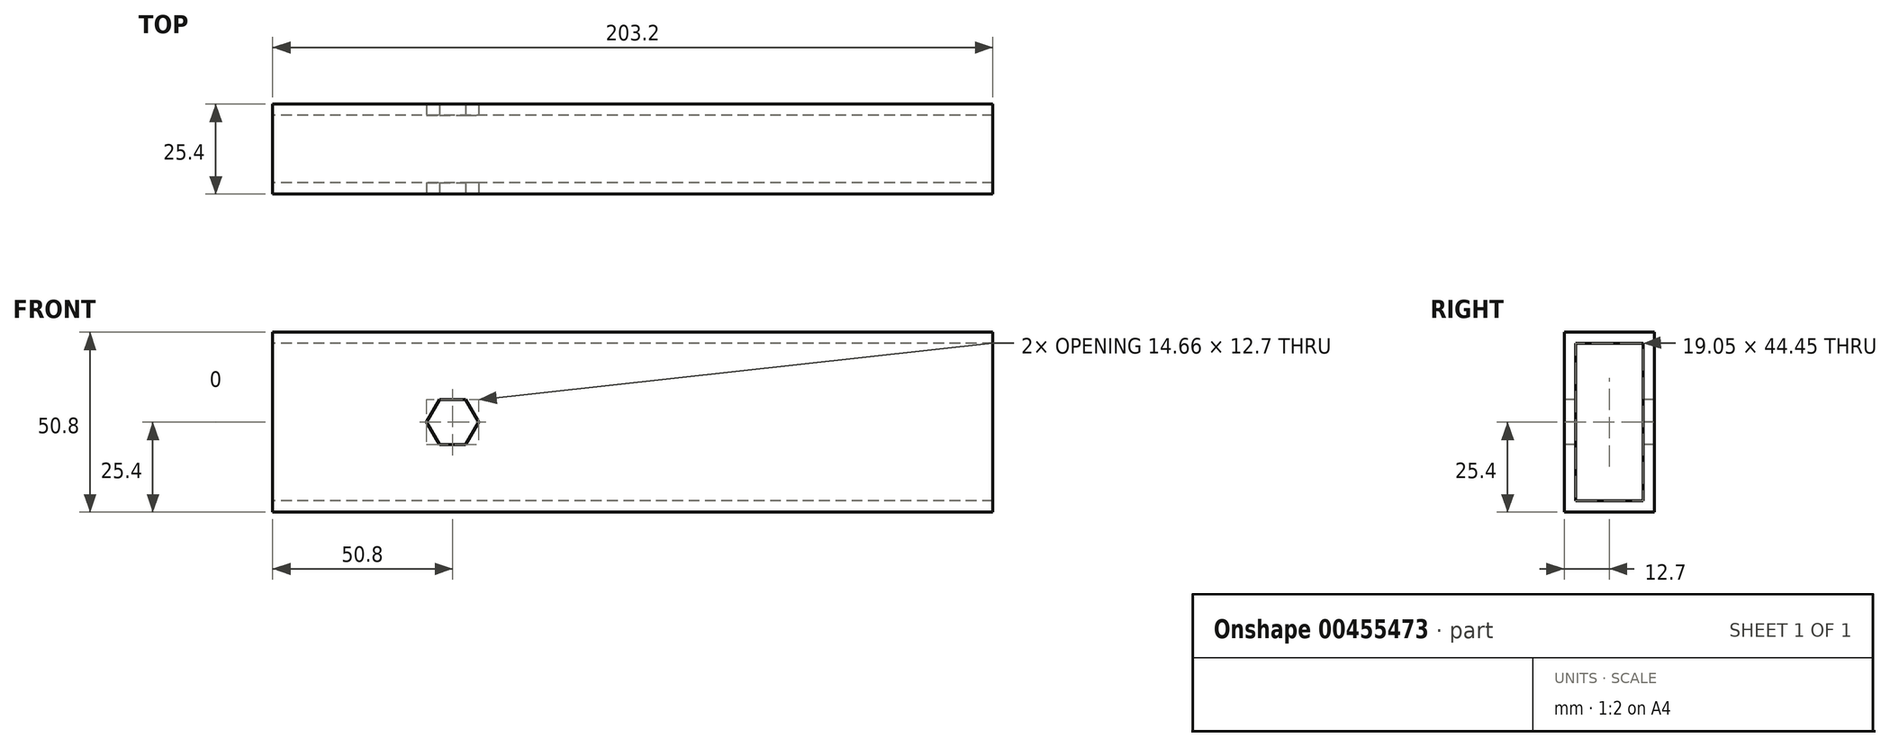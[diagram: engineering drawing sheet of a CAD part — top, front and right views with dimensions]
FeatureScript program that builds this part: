
annotation { "Feature Type Name" : "Feature", "Feature Type Description" : "" }
export const myFeature = defineFeature(function(context is Context, id is Id, definition is map)
    precondition{}
    {
        {
            var Q0;
            Q0=qCreatedBy(makeId("Front.planeOp"),FACE);
            var sketch = newSketch(context, id + "F0", { "sketchPlane" : qUnion([Q0])});
            skLineSegment(sketch, "E0.bottom", {"start": v(0, 0) * mm, "end": v(203.2, 0) * mm});
            skLineSegment(sketch, "E0.top", {"start": v(0, 50.8) * mm, "end": v(203.2, 50.8) * mm});
            skLineSegment(sketch, "E0.left", {"start": v(0, 0) * mm, "end": v(0, 50.8) * mm});
            skLineSegment(sketch, "E0.right", {"start": v(203.2, 0) * mm, "end": v(203.2, 50.8) * mm});
            skSolve(sketch);
        }
        {
            var Q0;
            Q0 = qSketchRegion(id + "F0", true);
            extrude(context, id + "F1", {"entities" : qUnion([Q0]), "depth" : 25.4 * mm});
        }
        {
            var Q0;
            Q0=makeQuery(id+"F1.opExtrude","SWEPT_FACE",FACE,{"disambiguationData":[OSD([sQuery(id+"F0.wireOp",EDGE,"E0.left")])]});
            var sketch = newSketch(context, id + "F2", { "sketchPlane" : qUnion([Q0])});
            skLineSegment(sketch, "E1.bottom", {"start": v(22.23, 3.18) * mm, "end": v(3.18, 3.17) * mm});
            skLineSegment(sketch, "E1.top", {"start": v(22.22, 47.62) * mm, "end": v(3.17, 47.62) * mm});
            skLineSegment(sketch, "E1.left", {"start": v(22.23, 3.18) * mm, "end": v(22.22, 47.62) * mm});
            skLineSegment(sketch, "E1.right", {"start": v(3.18, 3.17) * mm, "end": v(3.17, 47.62) * mm});
            skSolve(sketch);
        }
        {
            var Q0;
            Q0=makeQuery(id+"F2.imprint","IMPRINT",FACE,{"disambiguationData":[TD([[makeQuery(id+"F2.imprint","IMPRINT",EDGE,{"derivedFrom":sQuery(id+"F2.wireOp",EDGE,"E1.bottom")}),-1.0]])]});
            extrude(context, id + "F3", {"entities" : qUnion([Q0]), "operationType" : NewBodyOperationType.REMOVE, "oppositeDirection" : true, "depth" : 304.8 * mm});
        }
        {
            var Q0;
            Q0=makeQuery(id+"F1.opExtrude","CAP_FACE",FACE,{"disambiguationData":[OSD([sQuery(id+"F0.wireOp",EDGE,"E0.bottom"),sQuery(id+"F0.wireOp",EDGE,"E0.top"),sQuery(id+"F0.wireOp",EDGE,"E0.left"),sQuery(id+"F0.wireOp",EDGE,"E0.right")])],"isStart":false});
            var sketch = newSketch(context, id + "F4", { "sketchPlane" : qUnion([Q0])});
            skPoint(sketch, "E2", {"position": v(50.8, 25.4) * mm});
            skCircle(sketch, "E3.cCircle", {"center": v(50.8, 25.4) * mm, "radius": 6.35 * mm, "construction": true});
            skLineSegment(sketch, "E3.0", {"start": v(47.13, 31.75) * mm, "end": v(54.47, 31.75) * mm});
            skLineSegment(sketch, "E3.1", {"start": v(54.47, 31.75) * mm, "end": v(58.13, 25.4) * mm});
            skLineSegment(sketch, "E3.2", {"start": v(58.13, 25.4) * mm, "end": v(54.47, 19.05) * mm});
            skLineSegment(sketch, "E3.3", {"start": v(54.47, 19.05) * mm, "end": v(47.13, 19.05) * mm});
            skLineSegment(sketch, "E3.4", {"start": v(47.13, 19.05) * mm, "end": v(43.47, 25.4) * mm});
            skLineSegment(sketch, "E3.5", {"start": v(43.47, 25.4) * mm, "end": v(47.13, 31.75) * mm});
            skPoint(sketch, "E3.0.midPoint", {"position": v(50.8, 31.75) * mm});
            skSolve(sketch);
        }
        {
            var Q0;
            Q0=makeQuery(id+"F4.imprint","IMPRINT",FACE,{"disambiguationData":[TD([[makeQuery(id+"F4.imprint","IMPRINT",EDGE,{"derivedFrom":sQuery(id+"F4.wireOp",EDGE,"E3.0")}),-1.0]])]});
            extrude(context, id + "F5", {"entities" : qUnion([Q0]), "operationType" : NewBodyOperationType.REMOVE, "oppositeDirection" : true, "depth" : 25.4 * mm});
        }
    });
